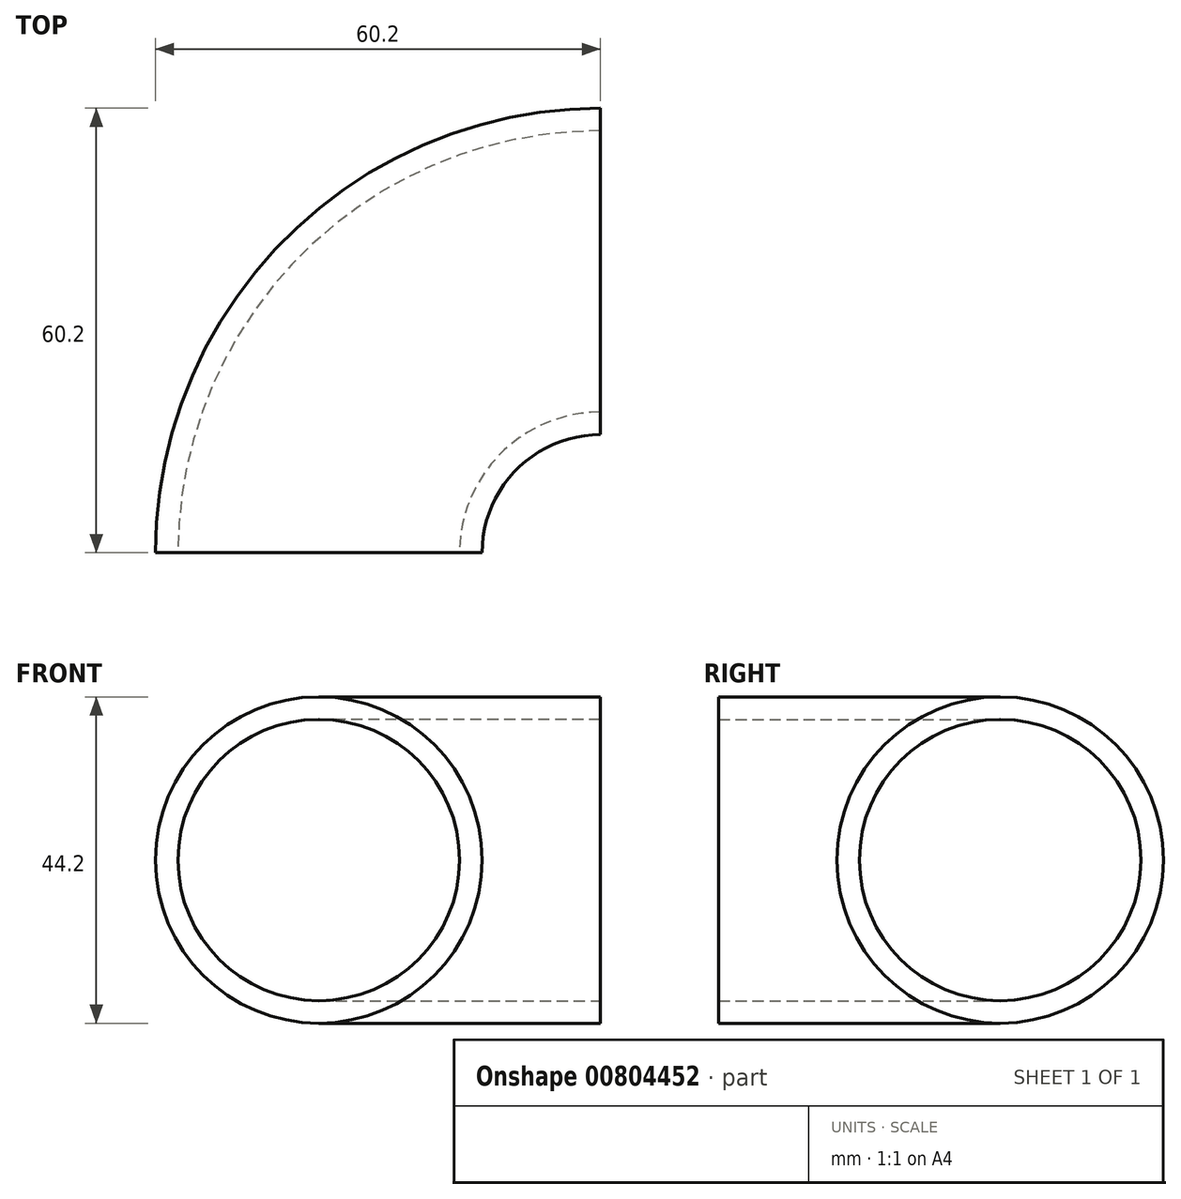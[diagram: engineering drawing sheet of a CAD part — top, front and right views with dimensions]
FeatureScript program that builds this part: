
annotation { "Feature Type Name" : "Feature", "Feature Type Description" : "" }
export const myFeature = defineFeature(function(context is Context, id is Id, definition is map)
    precondition{}
    {
        {
            var Q0;
            Q0=qCreatedBy(makeId("Top.planeOp"),FACE);
            var sketch = newSketch(context, id + "F0", { "sketchPlane" : qUnion([Q0])});
            skArc(sketch, "E0", {"start": v(0, 38.1) * mm, "mid": v(-26.94, 26.94) * mm, "end": v(-38.1, 0) * mm});
            skSolve(sketch);
        }
        {
            var Q0;
            Q0=qCreatedBy(makeId("Front.planeOp"),FACE);
            var sketch = newSketch(context, id + "F1", { "sketchPlane" : qUnion([Q0])});
            skLineSegment(sketch, "E1.0", {"start": v(0, 0) * mm, "end": v(-38.1, 0) * mm});
            skCircle(sketch, "E2", {"center": v(-38.1, 0) * mm, "radius": 22.1 * mm});
            skCircle(sketch, "E3", {"center": v(-38.1, 0) * mm, "radius": 19.05 * mm});
            skSolve(sketch);
        }
        {
            var Q0;
            Q0=makeQuery(id+"F1.imprint","IMPRINT",FACE,{"disambiguationData":[TD([[makeQuery(id+"F1.imprint","IMPRINT",EDGE,{"derivedFrom":sQuery(id+"F1.wireOp",EDGE,"E2")}),1.0]])]});
            var Q1;
            Q1=sQuery(id+"F0.wireOp",EDGE,"E0");
            sweep(context, id + "F2", {"profiles" : qUnion([Q0]), "path" : qUnion([Q1])});
        }
    });
